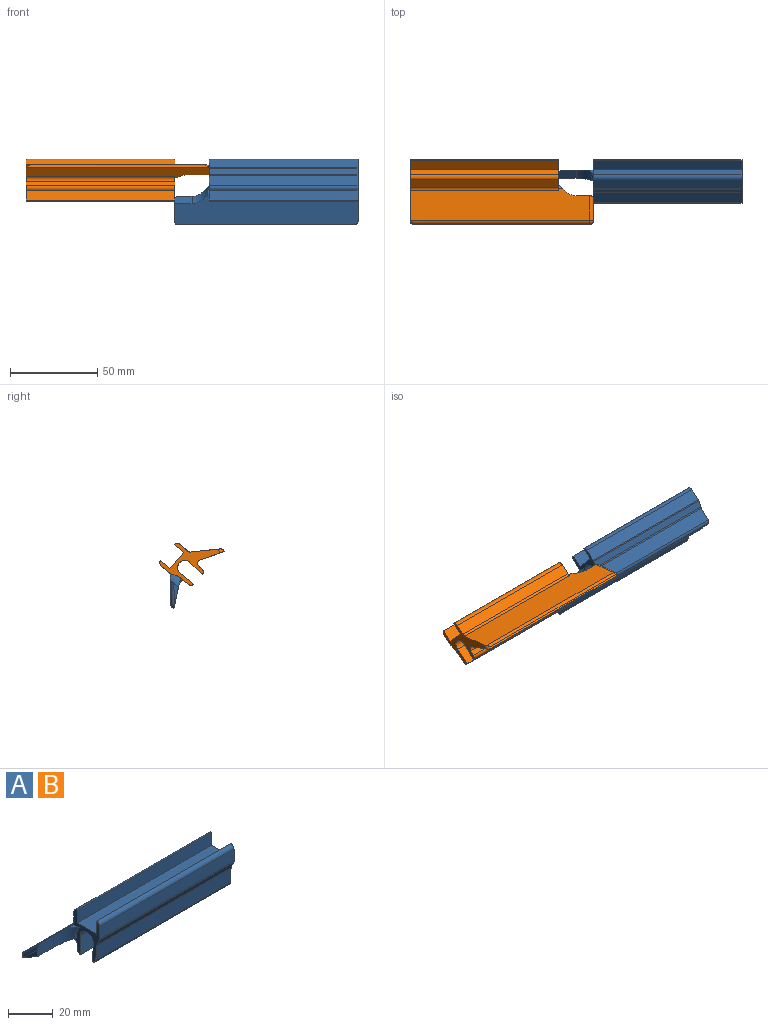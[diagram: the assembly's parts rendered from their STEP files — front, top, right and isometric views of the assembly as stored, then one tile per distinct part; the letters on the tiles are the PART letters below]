
ASSEMBLY  parts=2 mates=1
PART A: 37 faces, bbox 105x30.5x24 mm
  f0: plane 3.47x2.54mm, normal (0,0,1), area 3.8mm2, adj f12,f18,f19,f22
  f1: plane 85x6.63mm, normal (0,-1,0), area 563.5mm2, adj f17,f18,f31,f32
  f2: plane 85x3.48mm, normal (0,-0.92,-0.4), area 323.2mm2, adj f17,f18,f32,f33
  f3: plane 85x7.73mm, normal (0,-1,-0.05), area 657.5mm2, adj f17,f18,f33,f36
  f4: plane 85x0.15mm, normal (0,0,-1), area 12.9mm2, adj f5,f17,f18,f36
  f5: plane 85x9.99mm, normal (0,1,0.05), area 850mm2, adj f4,f6,f17,f18
  f6: cylinder r=4.2mm len=85mm, axis (-1,0,0), area 1121.5mm2, adj f5,f7,f17,f18
  f7: plane 85x9.99mm, normal (0,-1,0.05), area 850mm2, adj f6,f8,f17,f18
  f8: plane 85x0.15mm, normal (0,0,-1), area 12.9mm2, adj f7,f17,f18,f35
  f9: plane 85x2.89mm, normal (0,1,-0.05), area 246.4mm2, adj f17,f18,f34,f35
  f10: plane 105x15.74mm, normal (0,-0.48,-0.87), area 1524.8mm2, adj f11,f17,f18,f20,f21,f22,f23,f24
  f11: plane 101x0.95mm, normal (0,0.99,-0.13), area 96.8mm2, adj f10,f24,f25,f26
  f12: plane 103.04x13.33mm, normal (0,0.68,0.74), area 1734.2mm2, adj f0,f17,f18,f22,f23,f24,f26,f28
  f13: plane 85x6.17mm, normal (0,1,0), area 524.7mm2, adj f17,f18,f29,f30
  f14: plane 85x7mm, normal (0,-1,0), area 595mm2, adj f15,f17,f18,f30
  f15: plane 85x12.2mm, normal (0,0,1), area 1037mm2, adj f14,f16,f17,f18
  f16: plane 85x7mm, normal (0,1,0), area 595mm2, adj f15,f17,f18,f31
  f17: plane 28.46x23.24mm, normal (1,0,0), area 203.9mm2, adj f1,f2,f3,f4,f5,f6,f7,f8
  f18: plane 23.24x17.04mm, normal (-1,0,0), area 127.9mm2, adj f0,f1,f2,f3,f4,f5,f6,f7
  f19: cylinder r=6.25mm len=4.2mm, axis (1,0,0), area 2.7mm2, adj f0,f18,f20,f22
  f20: plane 2x0.94mm, normal (0,-1,0.05), area 1.8mm2, adj f10,f18,f19,f22
  f21: plane 9.02x8.49mm, normal (-1,0,0), area 16.6mm2, adj f10,f23,f25,f28
  f22: cylinder r=11.01mm len=9.99mm, axis (0,0,1), area 73.2mm2, adj f0,f10,f12,f19,f20,f23
  f23: plane 10x6.22mm, normal (0,-1,0), area 61mm2, adj f10,f12,f21,f22,f28
  f24: cylinder r=2mm len=3.64mm, axis (0,-0.13,-0.99), area 6.3mm2, adj f10,f11,f12,f17,f26
  f25: cylinder r=2mm len=2.11mm, axis (0,0.13,0.99), area 2.1mm2, adj f10,f11,f21,f27
  f26: cylinder r=2mm len=102.64mm, axis (-1,0,0), area 195.6mm2, adj f11,f12,f24,f27
  f27: sphere r=2mm, area 3.8mm2, adj f25,f26,f28
  f28: cylinder r=2mm len=11.73mm, axis (0,-0.74,0.68), area 42.2mm2, adj f12,f21,f23,f27
  f29: cylinder r=2mm len=85mm, axis (-1,0,0), area 140.5mm2, adj f12,f13,f17,f18
  f30: cylinder r=2mm len=85mm, axis (1,0,0), area 267mm2, adj f13,f14,f17,f18
  f31: cylinder r=2mm len=85mm, axis (-1,0,0), area 267mm2, adj f1,f16,f17,f18
  f32: cylinder r=2mm len=85mm, axis (-1,0,0), area 70.5mm2, adj f1,f2,f17,f18
  f33: cylinder r=2mm len=85mm, axis (-1,0,0), area 61.6mm2, adj f2,f3,f17,f18
  f34: cylinder r=2mm len=85mm, axis (-1,0,0), area 344.2mm2, adj f9,f10,f17,f18
  f35: cylinder r=2mm len=85mm, axis (1,0,0), area 258.1mm2, adj f8,f9,f17,f18
  f36: cylinder r=2mm len=85mm, axis (-1,0,0), area 258.1mm2, adj f3,f4,f17,f18
PART B: same geometry as A
PLACE A rot(axis=(-1,0,0),48.7deg) t=(-174.03,-26.77,-8.52)mm
PLACE B rot(axis=(0,-0.41,-0.91),180deg) t=(-194.03,-26.77,-8.52)mm
MATE fastened B.f22 <-> A.f22  axis (0,0.75,0.66) through (-184.03,-26.98,-8.7)mm
